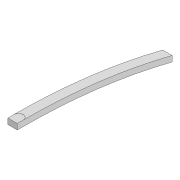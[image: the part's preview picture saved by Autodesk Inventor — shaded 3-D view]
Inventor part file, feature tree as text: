
AUTODESK INVENTOR PART (.ipt)
format: ipt  version: 2022 (Build 260153000, 153)  size: 129,536 bytes
history: native  units: mm
features: extrude x3, sketch x3, projected_geometry x2, fillet x1
ambient origin geometry x8: Origin, YZ Plane, XZ Plane, XY Plane, X Axis, Y Axis, Z Axis, Center Point
bodies: Solid1 (feature_tree)
feature tree (9):
  extrude  "Extrusion1"  Depth=10.0mm
  extrude  "Extrusion2"  Depth=40.0mm
  fillet  "Fillet1"  Radius=140.0mm
  extrude  "Extrusion3"  Depth=10.0mm TaperAngle=0.0deg
  sketch  "Sketch1"  dims[d0=180.0mm d1=10.0mm]
  sketch  "Sketch2"  dims[d2=3.3mm d3=40.0mm d5=140.0mm]
  projected_geometry  "Projected Loop1"
  projected_geometry  "Projected Loop2"
  sketch  "Sketch3"  dims[d6=3.3mm d7=6.0mm d8=0.0mm d9=6.0mm d10=498.004mm d11=90.0mm d12=10.0mm d13=0.0mm d14=2.0mm d15=100.0mm d16=0.0mm]
